# Revit family: Domotics-DomesticRanges-GEWISS-SYSTEM_CLIMATE-THERMOSTAT_3M
name_source: partatom
category: Apparecchi elettrici
revit_build: Autodesk Revit 2016 (Build: 20161004_0715(x64)
units: mm (PartAtom-declared; Revit-internal decimal feet)

## family parameters
Condiviso = Sì
Host = Superficie
Mantenere orientamento annotazione = Sì
Numero OmniClass = 23.80.50.11.14
Punto di calcolo locali = Sì
Quota connettore circolare = Usa diametro
Taglio con vuoti quando caricato = Sì
Tipo di parte = Normale
Titolo OmniClass = Switches

## types (4) — shared parameters
Bidimensionale = bidimensionale system termostato 3m : GW20853
Carico apparente = 0 VA
Catalogue = DOMOTICS
Catalogue Range = SYSTEM - DOMESTIC RANGE
Frequency = 50/60 Hz
IDF = 96866c00-4840-4755-bff9-7f97a67a1a05
IDT = 7f9c70d5-6711-49c2-b504-fcfc7c6bc753
Immagine tipo = GW21853.jpg
Larghezza termostato = 69 mm  [stored 0.226378 ft]
N. poli = 1
No. SYSTEM modules = 3
Produttore = GEWISS S.p.A.
Prospetto di default = 1219 mm
SEO = Thermostat
Simbolo = SIMBOLO TERMOSTATO SYSTEM : TERMOSTATO
Technical sheet = https://www.gewiss.com
Temperature adjustment = From +5°C to +30°C
Tipo = SYSTEM TERMOSTATO 3M_BASE : GW21853 - Nero - Fan coil
URL = https://www.gewiss.com
Version file RFA = 19.4
Volt = 230 V
Voltage = 230V ac
Voltage: = 230V ac

## per-type parameters (varying)
| type | Colour | Description. | Descrizione | EAN code | Electrocod | Modello | Output fan | Output solenoid | Regulation field | Regulation field: |
| GW20852 - Elect.thermostat winter/summer white | White | Thermostat | ELECT.THERMOSTAT WINTER/SUMMER SY/WT | 8011564109681 | 1734 | GW20852 |  |  |  |  |
| GW21852 - Elect.thermostat winter/summer black | Black | Thermostat | ELECT.THERMOSTAT WINTER/SUMMER SY/BK | 8011564129580 | 1734 | GW21852 |  |  |  |  |
| GW21853 - Electr.thermostat for fan-coil black | Black | FAN COIL thermostat | ELECTR.THERMOSTAT FOR FAN-COIL SY/BK | 8011564129597 | 1734 | GW21853 | Three way switch 1P | Relay NO/NC | +5° C / +30° C | +5° C / +30° C |
| GW20853 - Electr.thermostat for fan-coil white | White | FAN COIL thermostat | ELECTR.THERMOSTAT FOR FAN-COIL SY/WT | 8011564110915 | 1434 | GW20853 | Three way switch 1P | Relay NO/NC | +5° C / +30° C | +5° C / +30° C |

note: [stored X ft] marks values corroborated as IEEE doubles in the binary element streams (Revit-internal decimal feet)

## geometry (parser evidence)
native form markers: Sweep x2
no freeform markers — native parametric forms only
